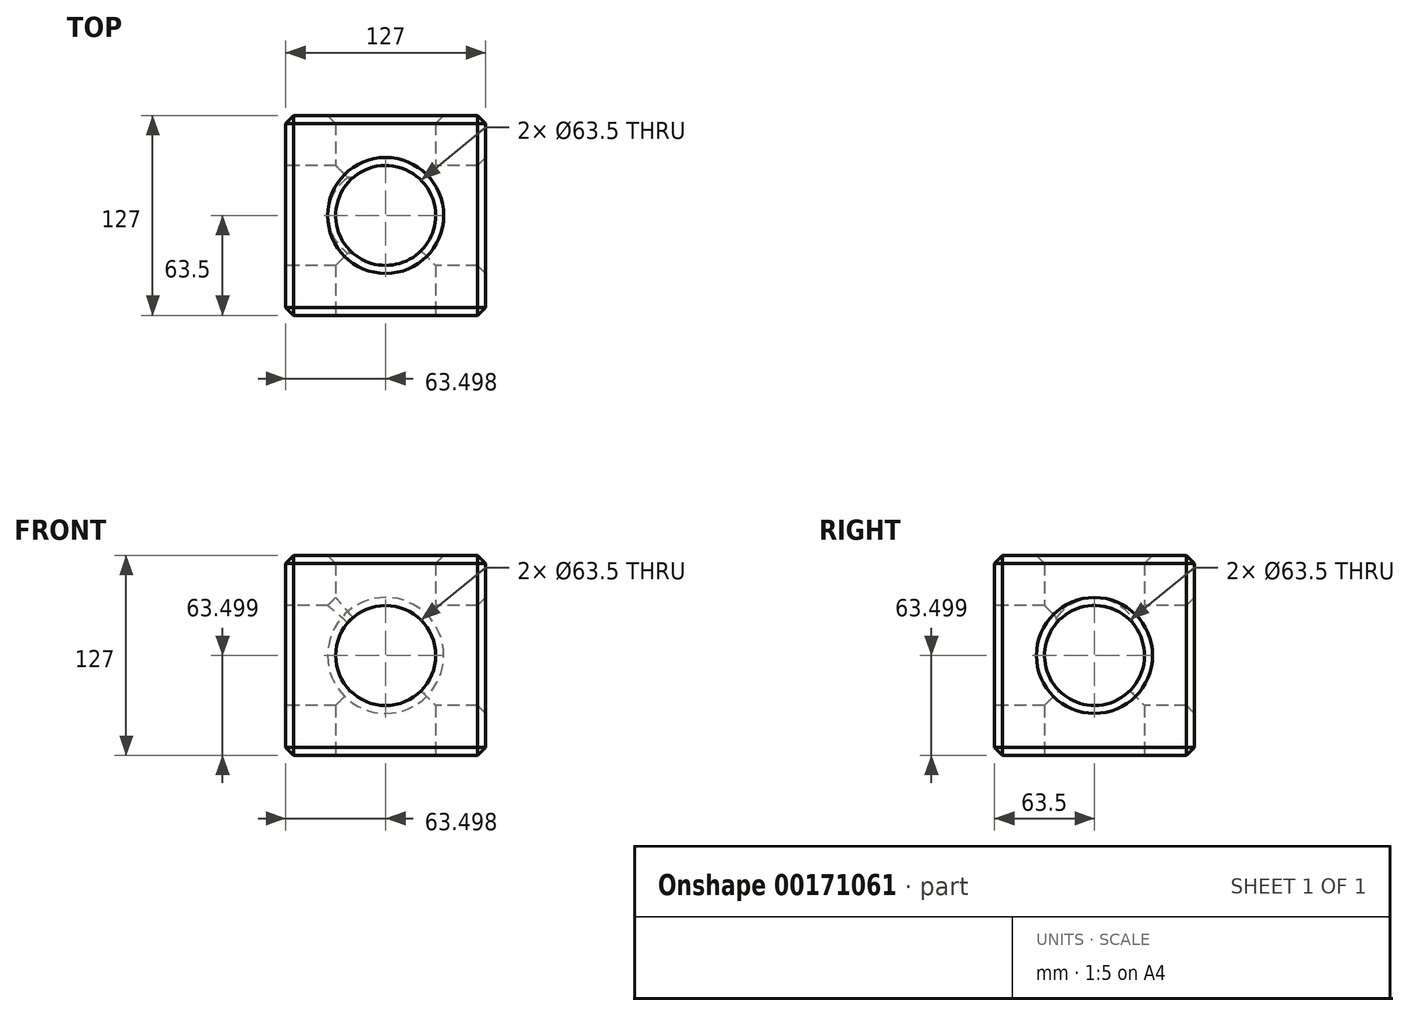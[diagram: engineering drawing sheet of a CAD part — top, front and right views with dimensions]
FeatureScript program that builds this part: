
annotation { "Feature Type Name" : "Feature", "Feature Type Description" : "" }
export const myFeature = defineFeature(function(context is Context, id is Id, definition is map)
    precondition{}
    {
        {
            var Q0;
            Q0=qCreatedBy(makeId("Front.planeOp"),FACE);
            var sketch = newSketch(context, id + "F0", { "sketchPlane" : qUnion([Q0])});
            skLineSegment(sketch, "E0.bottom", {"start": v(-67.67, 56.23) * mm, "end": v(59.33, 56.23) * mm});
            skLineSegment(sketch, "E0.top", {"start": v(-67.67, -70.77) * mm, "end": v(59.33, -70.77) * mm});
            skLineSegment(sketch, "E0.left", {"start": v(-67.67, 56.23) * mm, "end": v(-67.67, -70.77) * mm});
            skLineSegment(sketch, "E0.right", {"start": v(59.33, 56.23) * mm, "end": v(59.33, -70.77) * mm});
            skSolve(sketch);
        }
        {
            var Q0;
            Q0 = qSketchRegion(id + "F0", true);
            extrude(context, id + "F1", {"entities" : qUnion([Q0]), "depth" : 127 * mm});
        }
        {
            var Q0;
            Q0=makeQuery(id+"F1.opExtrude","CAP_FACE",FACE,{"disambiguationData":[OSD([sQuery(id+"F0.wireOp",EDGE,"E0.bottom"),sQuery(id+"F0.wireOp",EDGE,"E0.top"),sQuery(id+"F0.wireOp",EDGE,"E0.left"),sQuery(id+"F0.wireOp",EDGE,"E0.right")])],"isStart":false});
            var sketch = newSketch(context, id + "F2", { "sketchPlane" : qUnion([Q0])});
            skLineSegment(sketch, "E1", {"start": v(-67.67, 56.23) * mm, "end": v(59.33, -70.77) * mm, "construction": true});
            skCircle(sketch, "E2", {"center": v(-4.17, -7.27) * mm, "radius": 31.75 * mm});
            skSolve(sketch);
        }
        {
            var Q0;
            Q0=makeQuery(id+"F2.imprint","IMPRINT",FACE,{"disambiguationData":[TD([[makeQuery(id+"F2.imprint","IMPRINT",EDGE,{"derivedFrom":sQuery(id+"F2.wireOp",EDGE,"E2")}),1.0]])]});
            extrude(context, id + "F3", {"entities" : qUnion([Q0]), "operationType" : NewBodyOperationType.REMOVE, "endBound" : BoundingType.THROUGH_ALL, "oppositeDirection" : true, "depth" : 25.4 * mm});
        }
        {
            var Q0;
            Q0=makeQuery(id+"F1.opExtrude","SWEPT_FACE",FACE,{"disambiguationData":[OSD([sQuery(id+"F0.wireOp",EDGE,"E0.top")])]});
            var sketch = newSketch(context, id + "F4", { "sketchPlane" : qUnion([Q0])});
            skLineSegment(sketch, "E3", {"start": v(-67.67, 127) * mm, "end": v(59.33, 0) * mm, "construction": true});
            skCircle(sketch, "E4", {"center": v(-4.17, 63.5) * mm, "radius": 31.75 * mm});
            skSolve(sketch);
        }
        {
            var Q0;
            Q0=makeQuery(id+"F4.imprint","IMPRINT",FACE,{"disambiguationData":[TD([[makeQuery(id+"F4.imprint","IMPRINT",EDGE,{"derivedFrom":sQuery(id+"F4.wireOp",EDGE,"E4")}),1.0]])]});
            extrude(context, id + "F5", {"entities" : qUnion([Q0]), "operationType" : NewBodyOperationType.REMOVE, "endBound" : BoundingType.THROUGH_ALL, "oppositeDirection" : true, "depth" : 25.4 * mm});
        }
        {
            var Q0;
            Q0=makeQuery(id+"F1.opExtrude","SWEPT_FACE",FACE,{"disambiguationData":[OSD([sQuery(id+"F0.wireOp",EDGE,"E0.left")])]});
            var sketch = newSketch(context, id + "F6", { "sketchPlane" : qUnion([Q0])});
            skLineSegment(sketch, "E5", {"start": v(0, 56.23) * mm, "end": v(127, -70.77) * mm, "construction": true});
            skCircle(sketch, "E6", {"center": v(63.5, -7.27) * mm, "radius": 31.75 * mm});
            skSolve(sketch);
        }
        {
            var Q0;
            Q0=makeQuery(id+"F6.imprint","IMPRINT",FACE,{"disambiguationData":[TD([[makeQuery(id+"F6.imprint","IMPRINT",EDGE,{"derivedFrom":sQuery(id+"F6.wireOp",EDGE,"E6")}),1.0]])]});
            extrude(context, id + "F7", {"entities" : qUnion([Q0]), "operationType" : NewBodyOperationType.REMOVE, "endBound" : BoundingType.THROUGH_ALL, "oppositeDirection" : true, "depth" : 25.4 * mm});
        }
        {
            var Q0;
            Q0=makeQuery(id+"F1.opExtrude","CAP_EDGE",EDGE,{"disambiguationData":[OSD([sQuery(id+"F0.wireOp",EDGE,"E0.left")])],"isStart":true});
            var Q1;
            Q1=makeQuery(id+"F1.opExtrude","SWEPT_EDGE",EDGE,{"disambiguationData":[OSD([sQuery(id+"F0.wireOp",EDGE,"E0.top"),sQuery(id+"F0.wireOp",EDGE,"E0.left")])]});
            var Q2;
            Q2=makeQuery(id+"F1.opExtrude","CAP_EDGE",EDGE,{"disambiguationData":[OSD([sQuery(id+"F0.wireOp",EDGE,"E0.top")])],"isStart":true});
            var Q3;
            Q3=makeQuery(id+"F7.boolean.opBoolean","COPY",EDGE,{"derivedFrom":makeQuery(id+"F7.opExtrude","CAP_EDGE",EDGE,{"disambiguationData":[OSD([sQuery(id+"F6.wireOp",EDGE,"E6")])],"isStart":true})});
            var Q4;
            {var subQ0=makeQuery(id+"F5.opExtrude","SWEPT_FACE",FACE,{"disambiguationData":[OSD([sQuery(id+"F4.wireOp",EDGE,"E4")])]});Q4=makeQuery(id+"F7.boolean.opBoolean","INTERSECT",EDGE,{"disambiguationData":[OD(0.0)],"derivedFrom":[makeQuery(id+"F5.boolean.opBoolean","COPY",FACE,{"disambiguationData":[TD([makeQuery(id+"F1.opExtrude","SWEPT_FACE",FACE,{"disambiguationData":[OSD([sQuery(id+"F0.wireOp",EDGE,"E0.bottom")])]})])],"derivedFrom":subQ0}),makeQuery(id+"F7.opExtrude","SWEPT_FACE",FACE,{"disambiguationData":[OSD([sQuery(id+"F6.wireOp",EDGE,"E6")])]})]});}
            var Q5;
            Q5=makeQuery(id+"F1.opExtrude","SWEPT_EDGE",EDGE,{"disambiguationData":[OSD([sQuery(id+"F0.wireOp",EDGE,"E0.bottom"),sQuery(id+"F0.wireOp",EDGE,"E0.left")])]});
            var Q6;
            Q6=makeQuery(id+"F1.opExtrude","CAP_EDGE",EDGE,{"disambiguationData":[OSD([sQuery(id+"F0.wireOp",EDGE,"E0.left")])],"isStart":false});
            var Q7;
            Q7=makeQuery(id+"F3.boolean.opBoolean","COPY",EDGE,{"derivedFrom":makeQuery(id+"F3.opExtrude","CAP_EDGE",EDGE,{"disambiguationData":[OSD([sQuery(id+"F2.wireOp",EDGE,"E2")])],"isStart":true})});
            var Q8;
            Q8=makeQuery(id+"F5.boolean.opBoolean","COPY",EDGE,{"derivedFrom":makeQuery(id+"F5.opExtrude","CAP_EDGE",EDGE,{"disambiguationData":[OSD([sQuery(id+"F4.wireOp",EDGE,"E4")])],"isStart":true})});
            var Q9;
            Q9=makeQuery(id+"F1.opExtrude","SWEPT_EDGE",EDGE,{"disambiguationData":[OSD([sQuery(id+"F0.wireOp",EDGE,"E0.top"),sQuery(id+"F0.wireOp",EDGE,"E0.right")])]});
            var Q10;
            Q10=makeQuery(id+"F1.opExtrude","CAP_EDGE",EDGE,{"disambiguationData":[OSD([sQuery(id+"F0.wireOp",EDGE,"E0.right")])],"isStart":true});
            var Q11;
            Q11=makeQuery(id+"F7.boolean.opBoolean","INTERSECT",EDGE,{"derivedFrom":[makeQuery(id+"F1.opExtrude","SWEPT_FACE",FACE,{"disambiguationData":[OSD([sQuery(id+"F0.wireOp",EDGE,"E0.right")])]}),makeQuery(id+"F7.opExtrude","SWEPT_FACE",FACE,{"disambiguationData":[OSD([sQuery(id+"F6.wireOp",EDGE,"E6")])]})]});
            var Q12;
            Q12=makeQuery(id+"F1.opExtrude","SWEPT_EDGE",EDGE,{"disambiguationData":[OSD([sQuery(id+"F0.wireOp",EDGE,"E0.bottom"),sQuery(id+"F0.wireOp",EDGE,"E0.right")])]});
            var Q13;
            Q13=makeQuery(id+"F5.boolean.opBoolean","INTERSECT",EDGE,{"derivedFrom":[makeQuery(id+"F1.opExtrude","SWEPT_FACE",FACE,{"disambiguationData":[OSD([sQuery(id+"F0.wireOp",EDGE,"E0.bottom")])]}),makeQuery(id+"F5.opExtrude","SWEPT_FACE",FACE,{"disambiguationData":[OSD([sQuery(id+"F4.wireOp",EDGE,"E4")])]})]});
            var Q14;
            Q14=makeQuery(id+"F1.opExtrude","CAP_EDGE",EDGE,{"disambiguationData":[OSD([sQuery(id+"F0.wireOp",EDGE,"E0.bottom")])],"isStart":true});
            var Q15;
            Q15=makeQuery(id+"F3.boolean.opBoolean","INTERSECT",EDGE,{"derivedFrom":[makeQuery(id+"F1.opExtrude","CAP_FACE",FACE,{"disambiguationData":[OSD([sQuery(id+"F0.wireOp",EDGE,"E0.bottom"),sQuery(id+"F0.wireOp",EDGE,"E0.top"),sQuery(id+"F0.wireOp",EDGE,"E0.left"),sQuery(id+"F0.wireOp",EDGE,"E0.right")])],"isStart":true}),makeQuery(id+"F3.opExtrude","SWEPT_FACE",FACE,{"disambiguationData":[OSD([sQuery(id+"F2.wireOp",EDGE,"E2")])]})]});
            var Q16;
            Q16=makeQuery(id+"F1.opExtrude","CAP_EDGE",EDGE,{"disambiguationData":[OSD([sQuery(id+"F0.wireOp",EDGE,"E0.top")])],"isStart":false});
            var Q17;
            Q17=makeQuery(id+"F1.opExtrude","CAP_EDGE",EDGE,{"disambiguationData":[OSD([sQuery(id+"F0.wireOp",EDGE,"E0.right")])],"isStart":false});
            var Q18;
            Q18=makeQuery(id+"F1.opExtrude","CAP_EDGE",EDGE,{"disambiguationData":[OSD([sQuery(id+"F0.wireOp",EDGE,"E0.bottom")])],"isStart":false});
            chamfer(context, id + "F8", {"entities" : qUnion([Q0, Q1, Q2, Q3, Q4, Q5, Q6, Q7, Q8, Q9, Q10, Q11, Q12, Q13, Q14, Q15, Q16, Q17, Q18]), "width" : 5.08 * mm, "tangentPropagation" : true});
        }
    });
